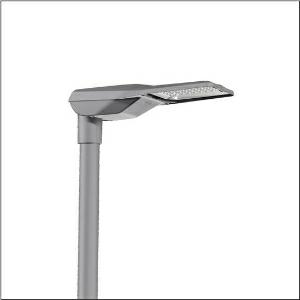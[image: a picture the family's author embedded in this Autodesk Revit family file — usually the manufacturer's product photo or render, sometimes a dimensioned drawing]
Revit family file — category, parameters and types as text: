
# Revit family: streetlight_sl_21_iq_mini___p0_8a_5xe2u31d08hb_de2c
name_source: partatom
category: Lighting Fixtures
units: mm (PartAtom-declared; Revit-internal decimal feet)

## family parameters
Cut with Voids When Loaded = No
Host = Face
Light Source = No
Part Type = Normal
Room Calculation Point = No
Round Connector Dimension = Use Diameter
Shared = No

## types (1)
- --- (1 x LED, 9540 lm, 70.9 W, 3000K)
    Apparent Load = 71 VA
    CIE Flux Codes = 33 69 96 100 100
    Color Rendering = 70
    Color Temperature = 3000K
    Default Elevation = 1800 mm
    Description = Streetlight SL 21 iQ mini, mast luminaire, primary light control with lens, of PMMA, primary optical cover: cover, of toughened safety glass, transparent, light distribution: P0.8a, light emission: direct distribution, primary light characteristic: asymmetric, installation type: post-top, side-entry, LED, High Power LED, rated luminous flux: 9.540lm, luminous efficacy: 135lm/W, light colour: 730, colour temperature: 3000K, control gear: iQ-Comfort, control: pre-setting: linear dimming characteristic, Auto-Match, Temp-Guard, Lumen-Switch, Night-Set, Smart-Wire, Light-Fading, Desk-Remote (wireless, voltage-free reading and setting of iQ features in the workshop via application-optimized NFC function/RFID function), optimised constant luminous flux control (CLO 2.0), mains connection: 220..240V, AC, 50/60Hz, start of lifetime: 71W, end of service life: 75W, reduction: 31W, luminaire housing, of diecast aluminium, powder-coated, Siteco® metallic grey (DB 702S), corrosivity category C5 mid according to DIN EN ISO 12944, please order mast flange separately, inclination adjustable: 0°, 5°, 10°, 15°, sealing non-destructively replaceable, multi-level sealing system, length: 628mm, width: 235mm, height: 110mm, mast flange for spigot size: 42mm (side-entry): 5XC10008XM4, 60/48mm (side-entry/post-top): 5XC10108XM2, 76/60mm (side-entry/post-top): 5XC10108XM1, mounting height: 4..8m, protection rating (complete): IP66, insulation class (complete): insulation class II (safety insulation), certification: CE, ENEC, ENEC+, VDE, impact resistance: IK10, permissible operating ambient temperature for outdoor applications: -40..+50°C, standard-compliant lighting for roads and squares, packaging unit: 1 piece

Light Distribution: P0.8a
    Height = 110 mm
    Lamp = 1 x LED
    Lamp Light Flux = 9540 lm
    Lamp Power = 70.9 W
    Lamp count = 1
    Length = 625 mm
    Luminous efficacy = 135 lm/W
    Manufacturer = Siteco
    ModVariant = No
    Model = 5XE2U31D08HB
    Number of Poles = 1
    OnlyDefault = Yes
    Power Factor = 1
    Product Name = Streetlight SL 21 iQ mini | P0.8a
    Product group = mast luminaire | pylon top
    ProductGroupID = 6100
    Protection Class = Protection class II
    Protection Degree = IP 66
    RLX_Detail_Level = 1
    RLX_Emergency_Light_Flux = 0 lm
    RLX_Emergency_Type = 0
    RLX_Emergency_Type_DB = No
    RlxData = <blob elided: 26101 chars, md5=3c591fc9>
    Socket = socket
    Standby Power = 0 W
    System Light Flux = 9540 lm
    System Power = 71 W
    Type Comments = factory setting: luminous flux: 100 % | dim-lin: 254 | 711 mA
    Type Image = l_1003519.jpg
    URL = http://relux.com
    VarID = @adj_072440
    Voltage = 0 V
    Weight = 0.00 kg
    Width = 234 mm

## geometry (parser evidence)
native form markers: Blend x4, Sweep x11
no freeform markers — native parametric forms only
